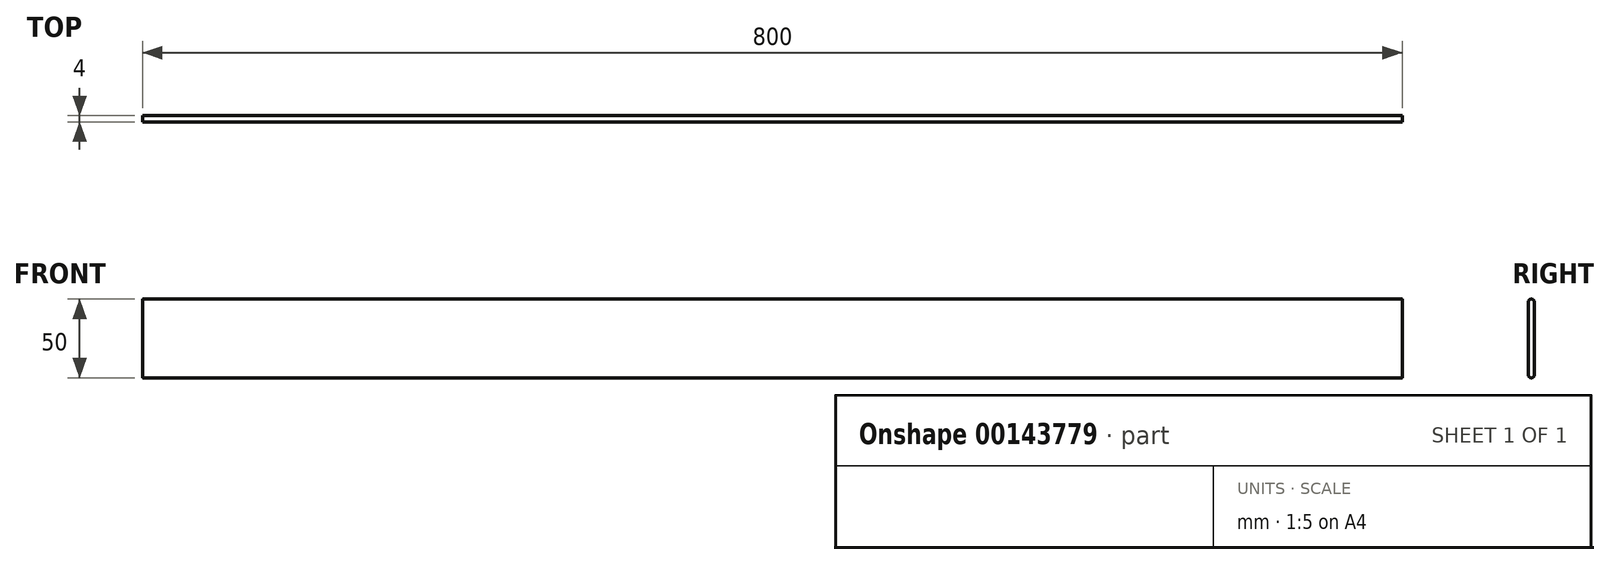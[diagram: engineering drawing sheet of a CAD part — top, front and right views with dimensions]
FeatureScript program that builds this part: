
annotation { "Feature Type Name" : "Feature", "Feature Type Description" : "" }
export const myFeature = defineFeature(function(context is Context, id is Id, definition is map)
    precondition{}
    {
        {
            var Q0;
            Q0=qCreatedBy(makeId("Right.planeOp"),FACE);
            var sketch = newSketch(context, id + "F0", { "sketchPlane" : qUnion([Q0])});
            skLineSegment(sketch, "E0.bottom", {"start": v(0, 50) * mm, "end": v(0, 50) * mm});
            skLineSegment(sketch, "E0.top", {"start": v(0, 0) * mm, "end": v(0, 0) * mm});
            skLineSegment(sketch, "E0.left", {"start": v(-2, 48) * mm, "end": v(-2, 2) * mm});
            skLineSegment(sketch, "E0.right", {"start": v(2, 48) * mm, "end": v(2, 2) * mm});
            skPoint(sketch, "E1.visualSharp", {"position": v(-2, 50) * mm});
            skArc(sketch, "E1.filletArc", {"start": v(0, 50) * mm, "mid": v(-1.41, 49.41) * mm, "end": v(-2, 48) * mm});
            skPoint(sketch, "E2.visualSharp", {"position": v(2, 50) * mm});
            skArc(sketch, "E2.filletArc", {"start": v(2, 48) * mm, "mid": v(1.41, 49.41) * mm, "end": v(0, 50) * mm});
            skPoint(sketch, "E3.visualSharp", {"position": v(-2, 0) * mm});
            skArc(sketch, "E3.filletArc", {"start": v(-2, 2) * mm, "mid": v(-1.41, 0.59) * mm, "end": v(0, 0) * mm});
            skPoint(sketch, "E4.visualSharp", {"position": v(2, 0) * mm});
            skArc(sketch, "E4.filletArc", {"start": v(0, 0) * mm, "mid": v(1.41, 0.59) * mm, "end": v(2, 2) * mm});
            skSolve(sketch);
        }
        {
            var Q0;
            Q0 = qSketchRegion(id + "F0", true);
            extrude(context, id + "F1", {"entities" : qUnion([Q0]), "endBound" : BoundingType.SYMMETRIC, "depth" : 800 * mm});
        }
    });
